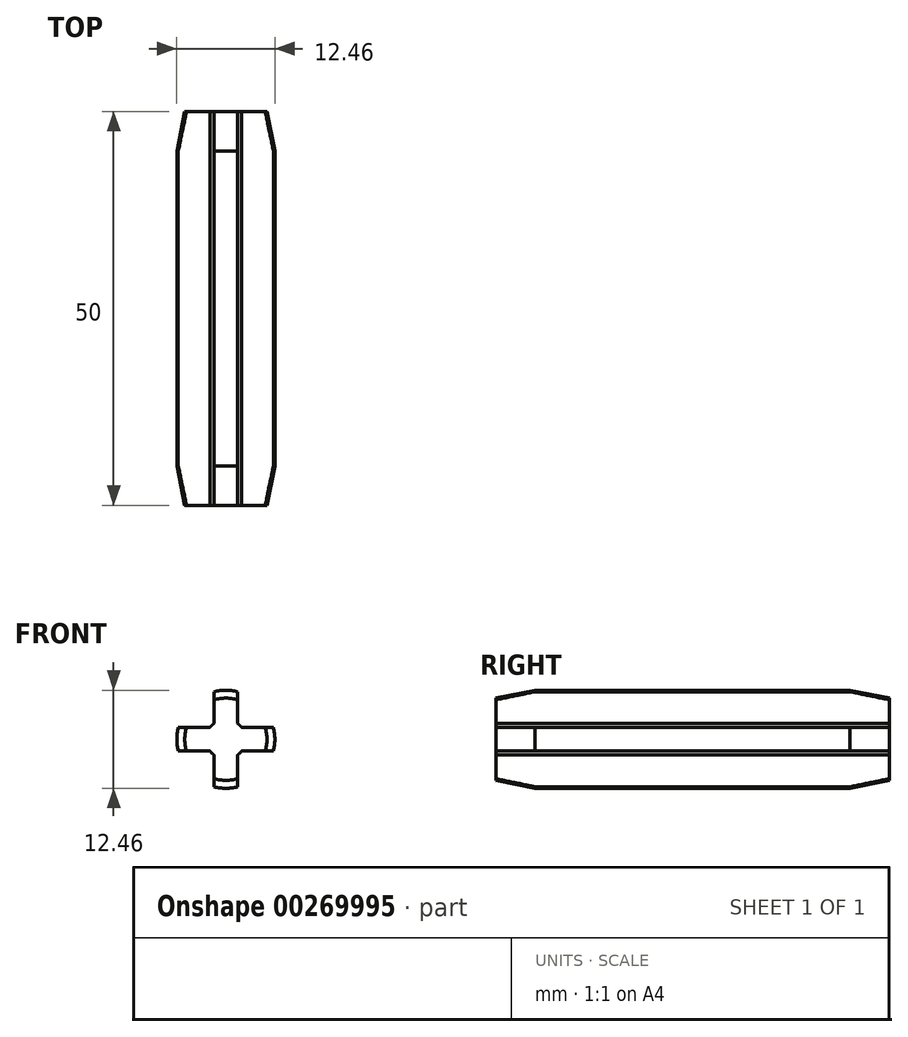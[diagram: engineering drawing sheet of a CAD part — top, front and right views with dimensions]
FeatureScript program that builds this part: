
annotation { "Feature Type Name" : "Feature", "Feature Type Description" : "" }
export const myFeature = defineFeature(function(context is Context, id is Id, definition is map)
    precondition{}
    {
        {
            var Q0;
            Q0=qCreatedBy(makeId("Front.planeOp"),FACE);
            var sketch = newSketch(context, id + "F0", { "sketchPlane" : qUnion([Q0])});
            skArc(sketch, "E0", {"start": v(-1.5, -6.04) * mm, "mid": v(0, -6.23) * mm, "end": v(1.5, -6.04) * mm});
            skArc(sketch, "E1", {"start": v(-1.5, 2) * mm, "mid": v(-1.77, 1.77) * mm, "end": v(-2, 1.5) * mm});
            skLineSegment(sketch, "E2.left", {"start": v(-1.5, 6.04) * mm, "end": v(-1.5, 2) * mm});
            skLineSegment(sketch, "E2.right", {"start": v(1.5, 6.04) * mm, "end": v(1.5, 2) * mm});
            skArc(sketch, "E3.trimOffspring", {"start": v(1.5, -2) * mm, "mid": v(1.77, -1.77) * mm, "end": v(2, -1.5) * mm});
            skLineSegment(sketch, "E4.bottom", {"start": v(-6.04, 1.5) * mm, "end": v(-2, 1.5) * mm});
            skLineSegment(sketch, "E4.top", {"start": v(-6.04, -1.5) * mm, "end": v(-2, -1.5) * mm});
            skLineSegment(sketch, "E5.trimOffspring", {"start": v(1.5, -2) * mm, "end": v(1.5, -6.04) * mm});
            skLineSegment(sketch, "E6.trimOffspring", {"start": v(2, 1.5) * mm, "end": v(6.04, 1.5) * mm});
            skLineSegment(sketch, "E7.trimOffspring", {"start": v(-1.5, -2) * mm, "end": v(-1.5, -6.04) * mm});
            skLineSegment(sketch, "E8.trimOffspring", {"start": v(2, -1.5) * mm, "end": v(6.04, -1.5) * mm});
            skArc(sketch, "E9.trimOffspring", {"start": v(2, 1.5) * mm, "mid": v(1.77, 1.77) * mm, "end": v(1.5, 2) * mm});
            skArc(sketch, "E10.trimOffspring", {"start": v(-2, -1.5) * mm, "mid": v(-1.77, -1.77) * mm, "end": v(-1.5, -2) * mm});
            skArc(sketch, "E11.trimOffspring", {"start": v(-6.04, 1.5) * mm, "mid": v(-6.23, 0) * mm, "end": v(-6.04, -1.5) * mm});
            skArc(sketch, "E12.trimOffspring", {"start": v(1.5, 6.04) * mm, "mid": v(0, 6.23) * mm, "end": v(-1.5, 6.04) * mm});
            skArc(sketch, "E13.trimOffspring", {"start": v(6.04, -1.5) * mm, "mid": v(6.23, 0) * mm, "end": v(6.04, 1.5) * mm});
            skSolve(sketch);
        }
        {
            var Q0;
            Q0=makeQuery(id+"F0.imprint","IMPRINT",FACE,{"disambiguationData":[TD([[makeQuery(id+"F0.imprint","IMPRINT",EDGE,{"derivedFrom":sQuery(id+"F0.wireOp",EDGE,"E0")}),1.0]])]});
            extrude(context, id + "F1", {"entities" : qUnion([Q0]), "depth" : 25 * mm, "offsetDistance" : 25 * mm, "hasSecondDirection" : true, "secondDirectionOppositeDirection" : true, "secondDirectionDepth" : 25 * mm});
        }
        {
            var Q0;
            Q0=makeQuery(id+"F1.opExtrude","CAP_EDGE",EDGE,{"disambiguationData":[OSD([sQuery(id+"F0.wireOp",EDGE,"E12.trimOffspring")])],"isStart":false});
            var Q1;
            Q1=makeQuery(id+"F1.opExtrude","CAP_EDGE",EDGE,{"disambiguationData":[OSD([sQuery(id+"F0.wireOp",EDGE,"E13.trimOffspring")])],"isStart":false});
            var Q2;
            Q2=makeQuery(id+"F1.opExtrude","CAP_EDGE",EDGE,{"disambiguationData":[OSD([sQuery(id+"F0.wireOp",EDGE,"E0")])],"isStart":false});
            var Q3;
            Q3=makeQuery(id+"F1.opExtrude","CAP_EDGE",EDGE,{"disambiguationData":[OSD([sQuery(id+"F0.wireOp",EDGE,"E11.trimOffspring")])],"isStart":false});
            chamfer(context, id + "F2", {"entities" : qUnion([Q0, Q1, Q2, Q3]), "chamferType" : ChamferType.TWO_OFFSETS, "width1" : 1 * mm, "oppositeDirection" : false, "width2" : 5 * mm, "tangentPropagation" : true});
        }
        {
            var Q0;
            Q0=makeQuery(id+"F1.opExtrude","CAP_EDGE",EDGE,{"disambiguationData":[OSD([sQuery(id+"F0.wireOp",EDGE,"E12.trimOffspring")])],"isStart":true});
            var Q1;
            Q1=makeQuery(id+"F1.opExtrude","CAP_EDGE",EDGE,{"disambiguationData":[OSD([sQuery(id+"F0.wireOp",EDGE,"E13.trimOffspring")])],"isStart":true});
            var Q2;
            Q2=makeQuery(id+"F1.opExtrude","CAP_EDGE",EDGE,{"disambiguationData":[OSD([sQuery(id+"F0.wireOp",EDGE,"E11.trimOffspring")])],"isStart":true});
            var Q3;
            Q3=makeQuery(id+"F1.opExtrude","CAP_EDGE",EDGE,{"disambiguationData":[OSD([sQuery(id+"F0.wireOp",EDGE,"E0")])],"isStart":true});
            chamfer(context, id + "F3", {"entities" : qUnion([Q0, Q1, Q2, Q3]), "chamferType" : ChamferType.TWO_OFFSETS, "width1" : 5 * mm, "oppositeDirection" : false, "width2" : 1 * mm, "tangentPropagation" : true});
        }
    });
